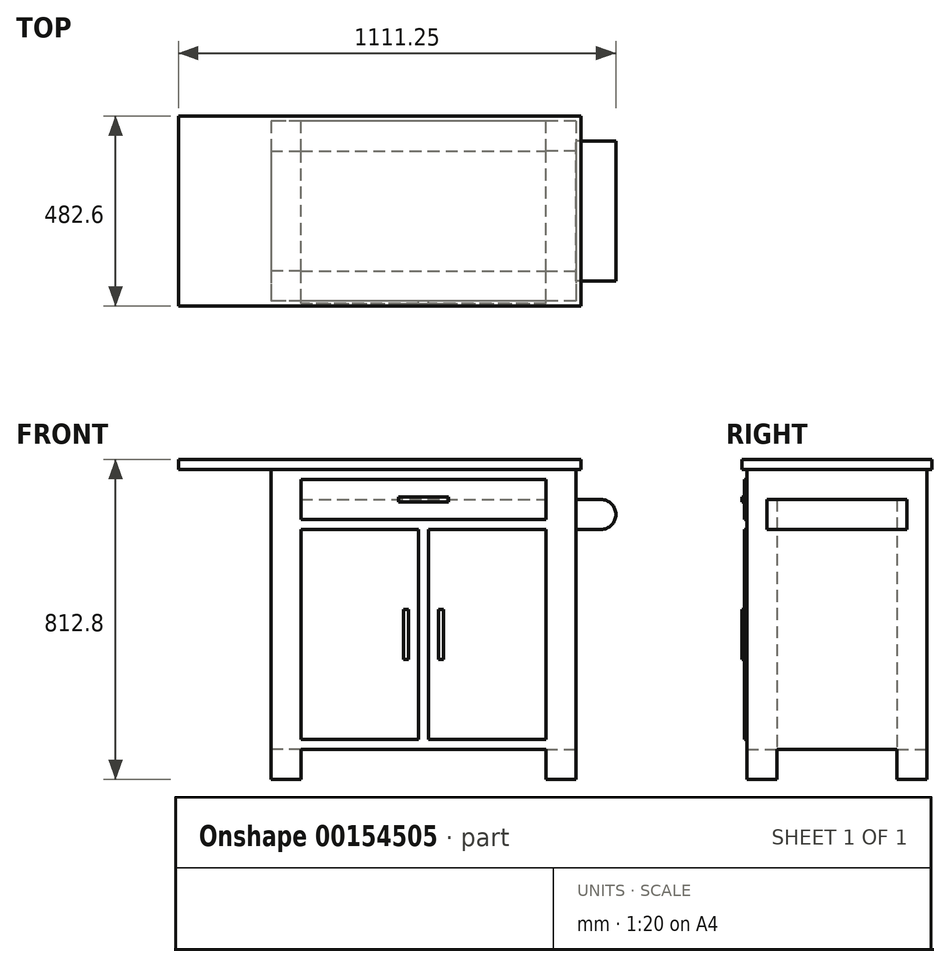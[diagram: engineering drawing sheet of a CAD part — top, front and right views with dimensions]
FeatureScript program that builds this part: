
annotation { "Feature Type Name" : "Feature", "Feature Type Description" : "" }
export const myFeature = defineFeature(function(context is Context, id is Id, definition is map)
    precondition{}
    {
        {
            var Q0;
            Q0=qCreatedBy(makeId("Top.planeOp"),FACE);
            var sketch = newSketch(context, id + "F0", { "sketchPlane" : qUnion([Q0])});
            skLineSegment(sketch, "E0.bottom", {"start": v(387.35, 228.6) * mm, "end": v(-387.35, 228.6) * mm});
            skLineSegment(sketch, "E0.top", {"start": v(387.35, -228.6) * mm, "end": v(-387.35, -228.6) * mm});
            skLineSegment(sketch, "E0.left", {"start": v(387.35, 228.6) * mm, "end": v(387.35, -228.6) * mm});
            skLineSegment(sketch, "E0.right", {"start": v(-387.35, 228.6) * mm, "end": v(-387.35, -228.6) * mm});
            skPoint(sketch, "E0.middle", {"position": v(0, 0) * mm});
            skLineSegment(sketch, "E1.bottom", {"start": v(400.05, 241.3) * mm, "end": v(-400.05, 241.3) * mm});
            skLineSegment(sketch, "E1.top", {"start": v(400.05, -241.3) * mm, "end": v(-400.05, -241.3) * mm});
            skLineSegment(sketch, "E1.left", {"start": v(400.05, 241.3) * mm, "end": v(400.05, -241.3) * mm});
            skLineSegment(sketch, "E1.right", {"start": v(-400.05, 241.3) * mm, "end": v(-400.05, -241.3) * mm});
            skLineSegment(sketch, "E2", {"start": v(311.15, 228.6) * mm, "end": v(311.15, 152.4) * mm});
            skLineSegment(sketch, "E3", {"start": v(311.15, 152.4) * mm, "end": v(387.35, 152.4) * mm});
            skLineSegment(sketch, "E4", {"start": v(387.35, -152.4) * mm, "end": v(311.15, -152.4) * mm});
            skLineSegment(sketch, "E5", {"start": v(311.15, -152.4) * mm, "end": v(311.15, -228.6) * mm});
            skLineSegment(sketch, "E6", {"start": v(-387.35, -152.4) * mm, "end": v(-311.15, -152.4) * mm});
            skLineSegment(sketch, "E7", {"start": v(-311.15, -152.4) * mm, "end": v(-311.15, -228.6) * mm});
            skLineSegment(sketch, "E8", {"start": v(-311.15, 228.6) * mm, "end": v(-311.15, 152.4) * mm});
            skLineSegment(sketch, "E9", {"start": v(-311.15, 152.4) * mm, "end": v(-387.35, 152.4) * mm});
            skSolve(sketch);
        }
        {
            var Q0;
            {var subQ3=sQuery(id+"F0.wireOp",EDGE,"E8");Q0=makeQuery(id+"F0.imprint","IMPRINT",FACE,{"disambiguationData":[TD([[makeQuery(id+"F0.imprint","IMPRINT",EDGE,{"derivedFrom":subQ3}),-1.0]])]});}
            var Q1;
            {var subQ4=sQuery(id+"F0.wireOp",EDGE,"E6");Q1=makeQuery(id+"F0.imprint","IMPRINT",FACE,{"disambiguationData":[TD([[makeQuery(id+"F0.imprint","IMPRINT",EDGE,{"derivedFrom":subQ4}),-1.0]])]});}
            var Q2;
            {var subQ4=sQuery(id+"F0.wireOp",EDGE,"E4");Q2=makeQuery(id+"F0.imprint","IMPRINT",FACE,{"disambiguationData":[TD([[makeQuery(id+"F0.imprint","IMPRINT",EDGE,{"derivedFrom":subQ4}),1.0]])]});}
            var Q3;
            {var subQ3=sQuery(id+"F0.wireOp",EDGE,"E2");Q3=makeQuery(id+"F0.imprint","IMPRINT",FACE,{"disambiguationData":[TD([[makeQuery(id+"F0.imprint","IMPRINT",EDGE,{"derivedFrom":subQ3}),1.0]])]});}
            extrude(context, id + "F1", {"entities" : qUnion([Q0, Q1, Q2, Q3]), "oppositeDirection" : true, "depth" : 812.8 * mm});
        }
        {
            var Q0;
            {var subQ3=sQuery(id+"F0.wireOp",EDGE,"E8");Q0=makeQuery(id+"F0.imprint","IMPRINT",FACE,{"disambiguationData":[TD([[makeQuery(id+"F0.imprint","IMPRINT",EDGE,{"derivedFrom":subQ3}),-1.0]])]});}
            var Q1;
            {var subQ5=sQuery(id+"F0.wireOp",EDGE,"E2");Q1=makeQuery(id+"F0.imprint","IMPRINT",FACE,{"disambiguationData":[TD([[makeQuery(id+"F0.imprint","IMPRINT",EDGE,{"derivedFrom":subQ5}),-1.0]])]});}
            var Q2;
            {var subQ4=sQuery(id+"F0.wireOp",EDGE,"E6");Q2=makeQuery(id+"F0.imprint","IMPRINT",FACE,{"disambiguationData":[TD([[makeQuery(id+"F0.imprint","IMPRINT",EDGE,{"derivedFrom":subQ4}),-1.0]])]});}
            var Q3;
            {var subQ4=sQuery(id+"F0.wireOp",EDGE,"E4");Q3=makeQuery(id+"F0.imprint","IMPRINT",FACE,{"disambiguationData":[TD([[makeQuery(id+"F0.imprint","IMPRINT",EDGE,{"derivedFrom":subQ4}),1.0]])]});}
            var Q4;
            {var subQ3=sQuery(id+"F0.wireOp",EDGE,"E2");Q4=makeQuery(id+"F0.imprint","IMPRINT",FACE,{"disambiguationData":[TD([[makeQuery(id+"F0.imprint","IMPRINT",EDGE,{"derivedFrom":subQ3}),1.0]])]});}
            extrude(context, id + "F2", {"entities" : qUnion([Q0, Q1, Q2, Q3, Q4]), "operationType" : NewBodyOperationType.ADD, "oppositeDirection" : true, "depth" : 736.6 * mm});
        }
        {
            var Q0;
            Q0=makeQuery(id+"F0.imprint","IMPRINT",FACE,{"disambiguationData":[TD([[makeQuery(id+"F0.imprint","IMPRINT",EDGE,{"derivedFrom":sQuery(id+"F0.wireOp",EDGE,"E1.bottom")}),1.0]])]});
            extrude(context, id + "F3", {"entities" : qUnion([Q0]), "operationType" : NewBodyOperationType.ADD, "oppositeDirection" : true, "depth" : 25.4 * mm});
        }
        {
            var Q0;
            {var subQ0=sQuery(id+"F0.wireOp",EDGE,"E0.left");Q0=makeQuery(id+"F2.boolean.opBoolean","MERGE",FACE,{"derivedFrom":[makeQuery(id+"F1.opExtrude","SWEPT_FACE",FACE,{"disambiguationData":[OSD([subQ0]),TDD([makeQuery(id+"F0.imprint","IMPRINT",EDGE,{"disambiguationData":[TD([[makeQuery(id+"F0.imprint","INTERSECT",VERTEX,{"derivedFrom":[sQuery(id+"F0.wireOp",EDGE,"E0.bottom"),subQ0]}),-1.0]])],"derivedFrom":subQ0})])]}),makeQuery(id+"F1.opExtrude","SWEPT_FACE",FACE,{"disambiguationData":[OSD([subQ0]),TDD([makeQuery(id+"F0.imprint","IMPRINT",EDGE,{"disambiguationData":[TD([[makeQuery(id+"F0.imprint","INTERSECT",VERTEX,{"derivedFrom":[sQuery(id+"F0.wireOp",EDGE,"E0.top"),subQ0]}),1.0]])],"derivedFrom":subQ0})])]}),makeQuery(id+"F2.opExtrude","SWEPT_FACE",FACE,{"disambiguationData":[OSD([subQ0])]})]});}
            var sketch = newSketch(context, id + "F4", { "sketchPlane" : qUnion([Q0])});
            skLineSegment(sketch, "E10.bottom", {"start": v(-177.8, -101.6) * mm, "end": v(177.8, -101.6) * mm});
            skLineSegment(sketch, "E10.top", {"start": v(-177.8, -177.8) * mm, "end": v(177.8, -177.8) * mm});
            skLineSegment(sketch, "E10.left", {"start": v(-177.8, -101.6) * mm, "end": v(-177.8, -177.8) * mm});
            skLineSegment(sketch, "E10.right", {"start": v(177.8, -101.6) * mm, "end": v(177.8, -177.8) * mm});
            skSolve(sketch);
        }
        {
            var Q0;
            Q0=makeQuery(id+"F4.imprint","IMPRINT",FACE,{"disambiguationData":[TD([[makeQuery(id+"F4.imprint","IMPRINT",EDGE,{"derivedFrom":sQuery(id+"F4.wireOp",EDGE,"E10.bottom")}),-1.0]])]});
            extrude(context, id + "F5", {"entities" : qUnion([Q0]), "operationType" : NewBodyOperationType.ADD, "depth" : 101.6 * mm});
        }
        {
            var Q0;
            Q0=makeQuery(id+"F5.opExtrude","CAP_EDGE",EDGE,{"disambiguationData":[OSD([sQuery(id+"F4.wireOp",EDGE,"E10.bottom")])],"isStart":false});
            var Q1;
            Q1=makeQuery(id+"F5.opExtrude","CAP_EDGE",EDGE,{"disambiguationData":[OSD([sQuery(id+"F4.wireOp",EDGE,"E10.top")])],"isStart":false});
            fillet(context, id + "F6", {"entities" : qUnion([Q0, Q1]), "radius" : 38.1 * mm, "tangentPropagation" : true, "allowEdgeOverflow" : false});
        }
        {
            var Q0;
            {var subQ0=sQuery(id+"F0.wireOp",EDGE,"E0.top");Q0=makeQuery(id+"F2.boolean.opBoolean","MERGE",FACE,{"derivedFrom":[makeQuery(id+"F1.opExtrude","SWEPT_FACE",FACE,{"disambiguationData":[OSD([subQ0]),TDD([makeQuery(id+"F0.imprint","IMPRINT",EDGE,{"disambiguationData":[TD([[makeQuery(id+"F0.imprint","INTERSECT",VERTEX,{"derivedFrom":[subQ0,sQuery(id+"F0.wireOp",EDGE,"E0.left")]}),-1.0]])],"derivedFrom":subQ0})])]}),makeQuery(id+"F1.opExtrude","SWEPT_FACE",FACE,{"disambiguationData":[OSD([subQ0]),TDD([makeQuery(id+"F0.imprint","IMPRINT",EDGE,{"disambiguationData":[TD([[makeQuery(id+"F0.imprint","INTERSECT",VERTEX,{"derivedFrom":[subQ0,sQuery(id+"F0.wireOp",EDGE,"E0.right")]}),1.0]])],"derivedFrom":subQ0})])]}),makeQuery(id+"F2.opExtrude","SWEPT_FACE",FACE,{"disambiguationData":[OSD([subQ0])]})]});}
            var sketch = newSketch(context, id + "F7", { "sketchPlane" : qUnion([Q0])});
            skLineSegment(sketch, "E11.bottom", {"start": v(-311.15, -50.8) * mm, "end": v(311.15, -50.8) * mm});
            skLineSegment(sketch, "E11.top", {"start": v(-311.15, -152.4) * mm, "end": v(311.15, -152.4) * mm});
            skLineSegment(sketch, "E11.left", {"start": v(-311.15, -50.8) * mm, "end": v(-311.15, -152.4) * mm});
            skLineSegment(sketch, "E11.right", {"start": v(311.15, -50.8) * mm, "end": v(311.15, -152.4) * mm});
            skLineSegment(sketch, "E12.bottom", {"start": v(311.15, -177.8) * mm, "end": v(12.7, -177.8) * mm});
            skLineSegment(sketch, "E12.top", {"start": v(311.15, -711.2) * mm, "end": v(12.7, -711.2) * mm});
            skLineSegment(sketch, "E12.left", {"start": v(311.15, -177.8) * mm, "end": v(311.15, -711.2) * mm});
            skLineSegment(sketch, "E12.right", {"start": v(12.7, -177.8) * mm, "end": v(12.7, -711.2) * mm});
            skLineSegment(sketch, "E13.bottom", {"start": v(-12.7, -711.2) * mm, "end": v(-311.15, -711.2) * mm});
            skLineSegment(sketch, "E13.top", {"start": v(-12.7, -177.8) * mm, "end": v(-311.15, -177.8) * mm});
            skLineSegment(sketch, "E13.left", {"start": v(-12.7, -711.2) * mm, "end": v(-12.7, -177.8) * mm});
            skLineSegment(sketch, "E13.right", {"start": v(-311.15, -711.2) * mm, "end": v(-311.15, -177.8) * mm});
            skLineSegment(sketch, "E14", {"start": v(0, -50.8) * mm, "end": v(0, -152.4) * mm, "construction": true});
            skLineSegment(sketch, "E15", {"start": v(-311.15, -444.5) * mm, "end": v(311.15, -444.5) * mm, "construction": true});
            skLineSegment(sketch, "E16.bottom", {"start": v(63.5, -95.25) * mm, "end": v(-63.5, -95.25) * mm});
            skLineSegment(sketch, "E16.top", {"start": v(63.5, -107.95) * mm, "end": v(-63.5, -107.95) * mm});
            skLineSegment(sketch, "E16.left", {"start": v(63.5, -95.25) * mm, "end": v(63.5, -107.95) * mm});
            skLineSegment(sketch, "E16.right", {"start": v(-63.5, -95.25) * mm, "end": v(-63.5, -107.95) * mm});
            skPoint(sketch, "E16.middle", {"position": v(0, -101.6) * mm});
            skLineSegment(sketch, "E17.bottom", {"start": v(-38.1, -381) * mm, "end": v(-50.8, -381) * mm});
            skLineSegment(sketch, "E17.top", {"start": v(-38.1, -508) * mm, "end": v(-50.8, -508) * mm});
            skLineSegment(sketch, "E17.left", {"start": v(-38.1, -381) * mm, "end": v(-38.1, -508) * mm});
            skLineSegment(sketch, "E17.right", {"start": v(-50.8, -381) * mm, "end": v(-50.8, -508) * mm});
            skPoint(sketch, "E17.middle", {"position": v(-44.45, -444.5) * mm});
            skLineSegment(sketch, "E18.bottom", {"start": v(50.8, -381) * mm, "end": v(38.1, -381) * mm});
            skLineSegment(sketch, "E18.top", {"start": v(50.8, -508) * mm, "end": v(38.1, -508) * mm});
            skLineSegment(sketch, "E18.left", {"start": v(50.8, -381) * mm, "end": v(50.8, -508) * mm});
            skLineSegment(sketch, "E18.right", {"start": v(38.1, -381) * mm, "end": v(38.1, -508) * mm});
            skPoint(sketch, "E18.middle", {"position": v(44.45, -444.5) * mm});
            skSolve(sketch);
        }
        {
            var Q0;
            Q0=makeQuery(id+"F7.imprint","IMPRINT",FACE,{"disambiguationData":[TD([[makeQuery(id+"F7.imprint","IMPRINT",EDGE,{"derivedFrom":sQuery(id+"F7.wireOp",EDGE,"E11.bottom")}),-1.0]])]});
            var Q1;
            Q1=makeQuery(id+"F7.imprint","IMPRINT",FACE,{"disambiguationData":[TD([[makeQuery(id+"F7.imprint","IMPRINT",EDGE,{"derivedFrom":sQuery(id+"F7.wireOp",EDGE,"E16.bottom")}),1.0]])]});
            var Q2;
            Q2=makeQuery(id+"F7.imprint","IMPRINT",FACE,{"disambiguationData":[TD([[makeQuery(id+"F7.imprint","IMPRINT",EDGE,{"derivedFrom":sQuery(id+"F7.wireOp",EDGE,"E12.bottom")}),1.0]])]});
            var Q3;
            Q3=makeQuery(id+"F7.imprint","IMPRINT",FACE,{"disambiguationData":[TD([[makeQuery(id+"F7.imprint","IMPRINT",EDGE,{"derivedFrom":sQuery(id+"F7.wireOp",EDGE,"E18.bottom")}),1.0]])]});
            var Q4;
            Q4=makeQuery(id+"F7.imprint","IMPRINT",FACE,{"disambiguationData":[TD([[makeQuery(id+"F7.imprint","IMPRINT",EDGE,{"derivedFrom":sQuery(id+"F7.wireOp",EDGE,"E17.bottom")}),1.0]])]});
            var Q5;
            Q5=makeQuery(id+"F7.imprint","IMPRINT",FACE,{"disambiguationData":[TD([[makeQuery(id+"F7.imprint","IMPRINT",EDGE,{"derivedFrom":sQuery(id+"F7.wireOp",EDGE,"E13.bottom")}),-1.0]])]});
            extrude(context, id + "F8", {"entities" : qUnion([Q0, Q1, Q2, Q3, Q4, Q5]), "operationType" : NewBodyOperationType.ADD, "depth" : 6.35 * mm});
        }
        {
            var Q0;
            Q0=makeQuery(id+"F7.imprint","IMPRINT",FACE,{"disambiguationData":[TD([[makeQuery(id+"F7.imprint","IMPRINT",EDGE,{"derivedFrom":sQuery(id+"F7.wireOp",EDGE,"E16.bottom")}),1.0]])]});
            var Q1;
            Q1=makeQuery(id+"F7.imprint","IMPRINT",FACE,{"disambiguationData":[TD([[makeQuery(id+"F7.imprint","IMPRINT",EDGE,{"derivedFrom":sQuery(id+"F7.wireOp",EDGE,"E17.bottom")}),1.0]])]});
            var Q2;
            Q2=makeQuery(id+"F7.imprint","IMPRINT",FACE,{"disambiguationData":[TD([[makeQuery(id+"F7.imprint","IMPRINT",EDGE,{"derivedFrom":sQuery(id+"F7.wireOp",EDGE,"E18.bottom")}),1.0]])]});
            extrude(context, id + "F9", {"entities" : qUnion([Q0, Q1, Q2]), "operationType" : NewBodyOperationType.ADD, "depth" : 12.7 * mm});
        }
        {
            var Q0;
            {var subQ0=sQuery(id+"F0.wireOp",EDGE,"E0.right");var subQ1=sQuery(id+"F0.wireOp",EDGE,"E0.left");var subQ2=sQuery(id+"F0.wireOp",EDGE,"E0.top");var subQ3=sQuery(id+"F0.wireOp",EDGE,"E0.bottom");Q0=makeQuery(id+"F3.boolean.opBoolean","MERGE",FACE,{"derivedFrom":[makeQuery(id+"F2.boolean.opBoolean","MERGE",FACE,{"derivedFrom":[makeQuery(id+"F1.opExtrude","CAP_FACE",FACE,{"disambiguationData":[OSD([subQ3,subQ1,sQuery(id+"F0.wireOp",EDGE,"E2"),sQuery(id+"F0.wireOp",EDGE,"E3")])],"isStart":true}),makeQuery(id+"F1.opExtrude","CAP_FACE",FACE,{"disambiguationData":[OSD([subQ3,subQ0,sQuery(id+"F0.wireOp",EDGE,"E8"),sQuery(id+"F0.wireOp",EDGE,"E9")])],"isStart":true}),makeQuery(id+"F1.opExtrude","CAP_FACE",FACE,{"disambiguationData":[OSD([subQ2,subQ1,sQuery(id+"F0.wireOp",EDGE,"E4"),sQuery(id+"F0.wireOp",EDGE,"E5")])],"isStart":true}),makeQuery(id+"F1.opExtrude","CAP_FACE",FACE,{"disambiguationData":[OSD([subQ2,subQ0,sQuery(id+"F0.wireOp",EDGE,"E6"),sQuery(id+"F0.wireOp",EDGE,"E7")])],"isStart":true}),makeQuery(id+"F2.opExtrude","CAP_FACE",FACE,{"disambiguationData":[OSD([subQ3,subQ2,subQ1,subQ0])],"isStart":true})]}),makeQuery(id+"F3.opExtrude","CAP_FACE",FACE,{"disambiguationData":[OSD([subQ3,subQ2,subQ1,subQ0,sQuery(id+"F0.wireOp",EDGE,"E1.bottom"),sQuery(id+"F0.wireOp",EDGE,"E1.top"),sQuery(id+"F0.wireOp",EDGE,"E1.left"),sQuery(id+"F0.wireOp",EDGE,"E1.right")])],"isStart":true})]});}
            var sketch = newSketch(context, id + "F10", { "sketchPlane" : qUnion([Q0])});
            skLineSegment(sketch, "E19.bottom", {"start": v(-400.05, 241.3) * mm, "end": v(-622.3, 241.3) * mm});
            skLineSegment(sketch, "E19.top", {"start": v(-400.05, -241.3) * mm, "end": v(-622.3, -241.3) * mm});
            skLineSegment(sketch, "E19.left", {"start": v(-400.05, 241.3) * mm, "end": v(-400.05, -241.3) * mm});
            skLineSegment(sketch, "E19.right", {"start": v(-622.3, 241.3) * mm, "end": v(-622.3, -241.3) * mm});
            skSolve(sketch);
        }
        {
            var Q0;
            Q0=makeQuery(id+"F10.imprint","IMPRINT",FACE,{"disambiguationData":[TD([[makeQuery(id+"F10.imprint","IMPRINT",EDGE,{"derivedFrom":sQuery(id+"F10.wireOp",EDGE,"E19.bottom")}),1.0]])]});
            var Q1;
            Q1=makeQuery(id+"F3.opExtrude","CAP_FACE",FACE,{"disambiguationData":[OSD([sQuery(id+"F0.wireOp",EDGE,"E0.bottom"),sQuery(id+"F0.wireOp",EDGE,"E0.top"),sQuery(id+"F0.wireOp",EDGE,"E0.left"),sQuery(id+"F0.wireOp",EDGE,"E0.right"),sQuery(id+"F0.wireOp",EDGE,"E1.bottom"),sQuery(id+"F0.wireOp",EDGE,"E1.top"),sQuery(id+"F0.wireOp",EDGE,"E1.left"),sQuery(id+"F0.wireOp",EDGE,"E1.right")])],"isStart":false});
            extrude(context, id + "F11", {"entities" : qUnion([Q0]), "operationType" : NewBodyOperationType.ADD, "endBound" : BoundingType.UP_TO_SURFACE, "oppositeDirection" : true, "endBoundEntityFace" : qUnion([Q1]), "depth" : 30.48 * mm});
        }
        {
            var Q0;
            Q0=makeQuery(id+"F2.opExtrude","CAP_FACE",FACE,{"disambiguationData":[OSD([sQuery(id+"F0.wireOp",EDGE,"E0.bottom"),sQuery(id+"F0.wireOp",EDGE,"E0.top"),sQuery(id+"F0.wireOp",EDGE,"E0.left"),sQuery(id+"F0.wireOp",EDGE,"E0.right")])],"isStart":false});
            var sketch = newSketch(context, id + "F12", { "sketchPlane" : qUnion([Q0])});
            skLineSegment(sketch, "E20.bottom", {"start": v(-311.15, 152.4) * mm, "end": v(311.15, 152.4) * mm});
            skLineSegment(sketch, "E20.top", {"start": v(-311.15, -152.4) * mm, "end": v(311.15, -152.4) * mm});
            skLineSegment(sketch, "E20.left", {"start": v(-311.15, 152.4) * mm, "end": v(-311.15, -152.4) * mm});
            skLineSegment(sketch, "E20.right", {"start": v(311.15, 152.4) * mm, "end": v(311.15, -152.4) * mm});
            skSolve(sketch);
        }
        {
            var Q0;
            Q0=makeQuery(id+"F12.imprint","IMPRINT",FACE,{"disambiguationData":[TD([[makeQuery(id+"F12.imprint","IMPRINT",EDGE,{"derivedFrom":sQuery(id+"F12.wireOp",EDGE,"E20.bottom")}),-1.0]])]});
            extrude(context, id + "F13", {"entities" : qUnion([Q0]), "operationType" : NewBodyOperationType.REMOVE, "oppositeDirection" : true, "depth" : 635 * mm});
        }
    });
